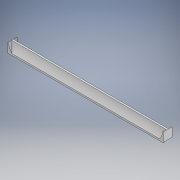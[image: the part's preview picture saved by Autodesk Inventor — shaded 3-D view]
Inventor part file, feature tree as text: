
AUTODESK INVENTOR PART (.ipt)
format: ipt  version: 2022.2 (Build 262287010, 287A)  size: 150,016 bytes
history: native  units: in
note: dims shown in document units (in); Inventor stores cm internally (conversion verified against a paired STEP export)
features: direct_edit x1, extrude x1, sketch x1, projected_geometry x1, other x1, revolve x1
ambient origin geometry x8: Origin, YZ Plane, XZ Plane, XY Plane, X Axis, Y Axis, Z Axis, Center Point
bodies: Solid1 (feature_tree)
feature tree (6):
  direct_edit  "Direct Edit1"
  extrude  "Extrusion1"  Depth=1.0in TaperAngle=0.0deg
  sketch  "Sketch1"  dims[d0=-1.2368in d1=1.0in d2=0.0in]
  projected_geometry  "Projected Loop1"
  other  "Transom (Center)"
  revolve  "Rotate1"  [1 undecoded]
note: 1 required parameter value undecoded (feature->parameter linkage not recoverable at this tier; creation-order binding heuristic only, values carry confidence <= 0.55)
